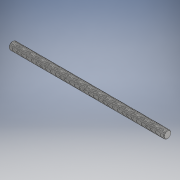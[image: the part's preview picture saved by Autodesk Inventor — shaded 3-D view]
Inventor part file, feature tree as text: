
AUTODESK INVENTOR PART (.ipt)
format: ipt  version: 2019 (Build 230136000, 136)  size: 2,279,936 bytes
history: native  units: mm
features: mirror x1
ambient origin geometry x8: Origin, YZ Plane, XZ Plane, XY Plane, X Axis, Y Axis, Z Axis, Center Point
bodies: Solid1 (feature_tree)
feature tree (1):
  mirror  "Mirror1"
